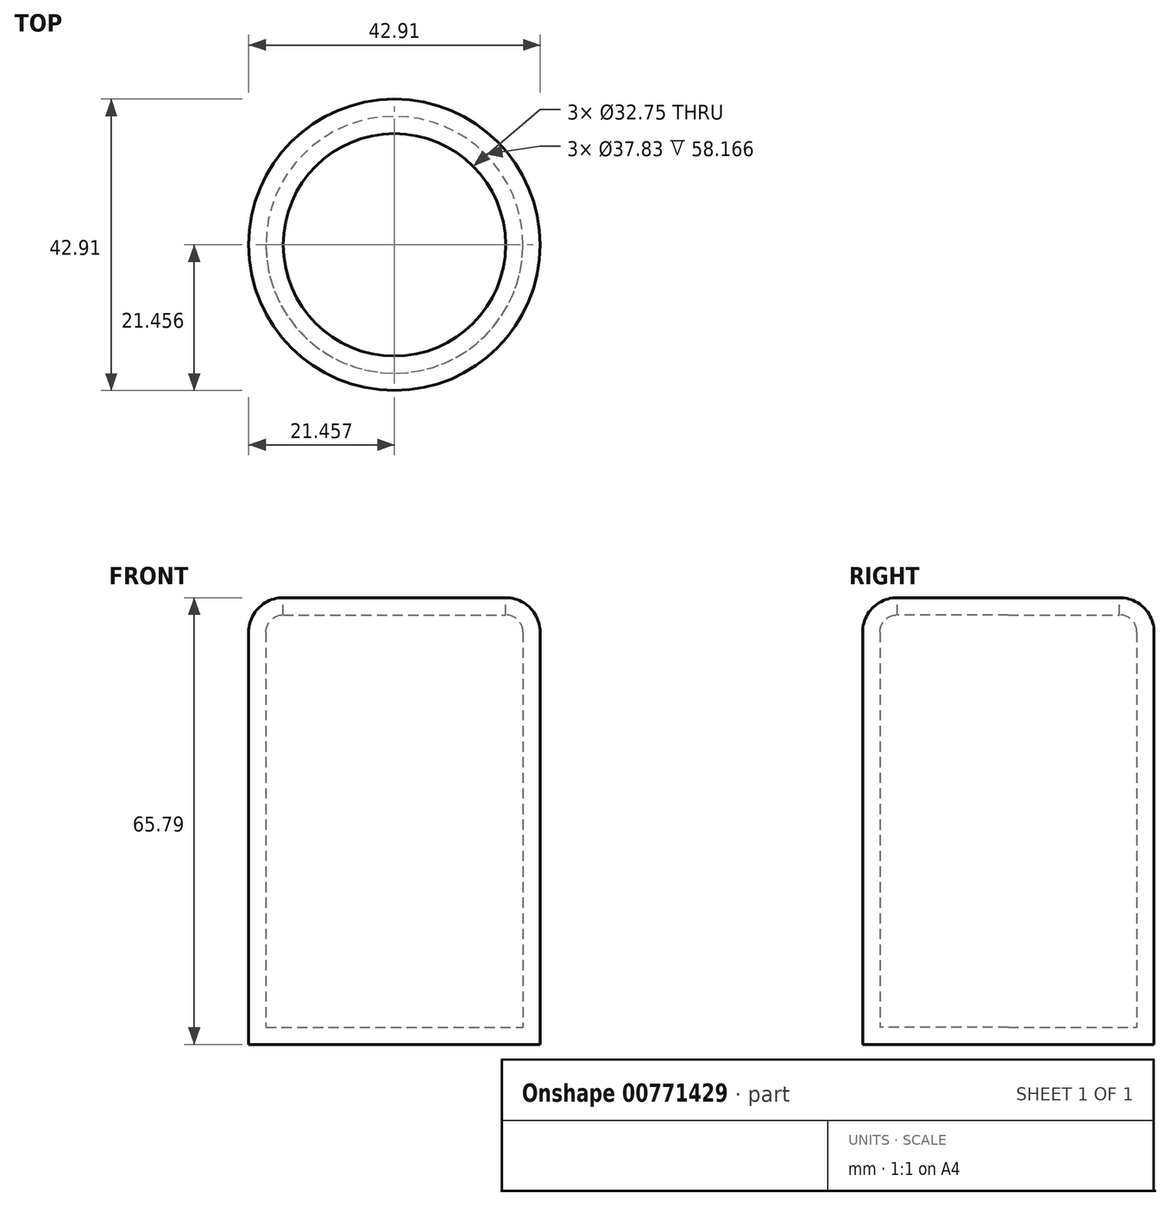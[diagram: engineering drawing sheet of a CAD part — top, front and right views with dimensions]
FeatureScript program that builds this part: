
annotation { "Feature Type Name" : "Feature", "Feature Type Description" : "" }
export const myFeature = defineFeature(function(context is Context, id is Id, definition is map)
    precondition{}
    {
        {
            var Q0;
            Q0=qCreatedBy(makeId("Top.planeOp"),FACE);
            var sketch = newSketch(context, id + "F0", { "sketchPlane" : qUnion([Q0])});
            skCircle(sketch, "E0", {"center": v(-44.3, 29.35) * mm, "radius": 21.45 * mm});
            skSolve(sketch);
        }
        {
            var Q0;
            Q0 = qSketchRegion(id + "F0", true);
            extrude(context, id + "F1", {"entities" : qUnion([Q0]), "depth" : 65.8 * mm, "offsetDistance" : 25.4 * mm});
        }
        {
            var Q0;
            Q0=makeQuery(id+"F1.opExtrude","CAP_FACE",FACE,{"disambiguationData":[OSD([sQuery(id+"F0.wireOp",EDGE,"E0")])],"isStart":false});
            fillet(context, id + "F2", {"entities" : qUnion([Q0]), "radius" : 5.08 * mm, "tangentPropagation" : true, "allowEdgeOverflow" : false});
        }
        {
            var Q0;
            Q0=makeQuery(id+"F1.opExtrude","CAP_FACE",FACE,{"disambiguationData":[OSD([sQuery(id+"F0.wireOp",EDGE,"E0")])],"isStart":false});
            shell(context, id + "F3", {"entities" : qUnion([Q0]), "thickness" : 2.54 * mm});
        }
    });
